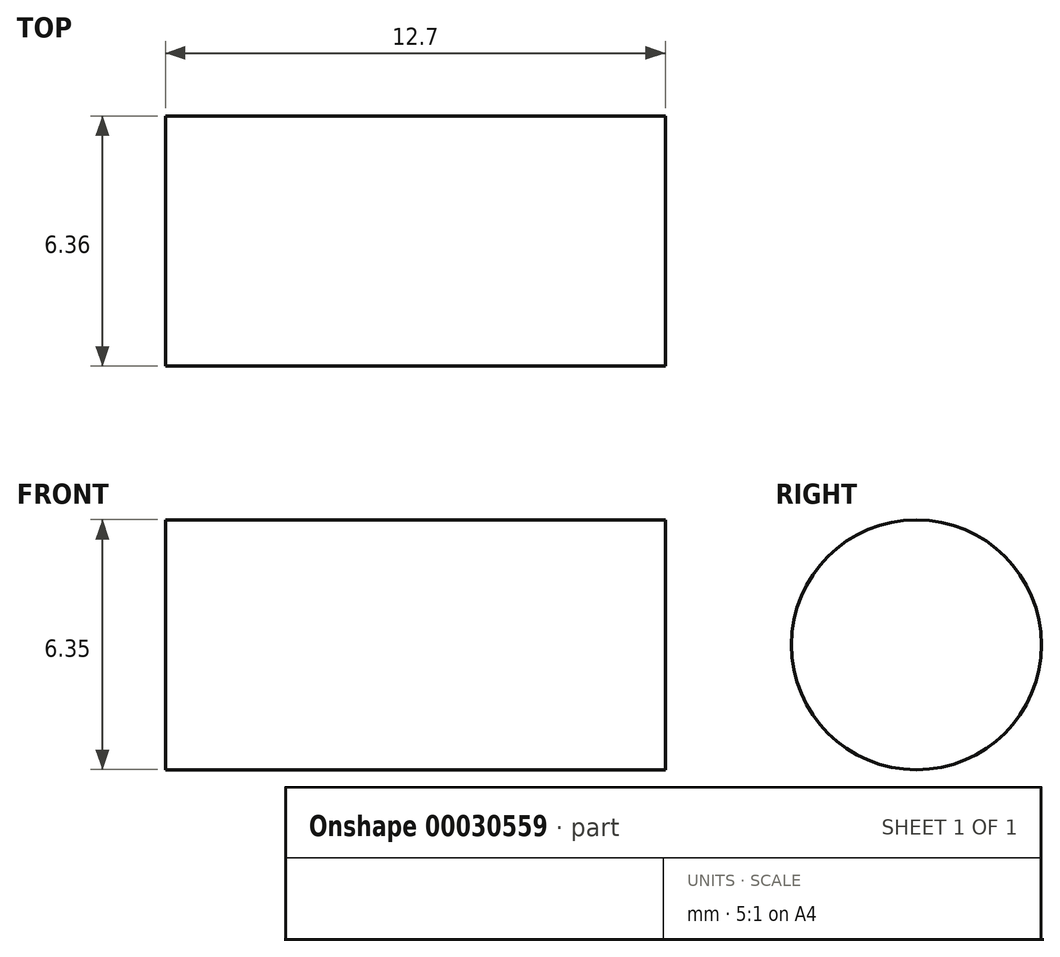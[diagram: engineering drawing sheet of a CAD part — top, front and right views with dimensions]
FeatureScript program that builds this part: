
annotation { "Feature Type Name" : "Feature", "Feature Type Description" : "" }
export const myFeature = defineFeature(function(context is Context, id is Id, definition is map)
    precondition{}
    {
        {
            var Q0;
            Q0=qCreatedBy(makeId("Front.planeOp"),FACE);
            var sketch = newSketch(context, id + "F0", { "sketchPlane" : qUnion([Q0])});
            skLineSegment(sketch, "E0", {"start": v(-13.32, -0.53) * mm, "end": v(-21.67, -0.53) * mm});
            skLineSegment(sketch, "E1", {"start": v(-13.32, 2.65) * mm, "end": v(-13.32, -0.53) * mm});
            skPoint(sketch, "E2.endSnap0", {"position": v(-0.62, -0.53) * mm});
            skLineSegment(sketch, "E2", {"start": v(-13.32, -0.53) * mm, "end": v(19.02, -0.53) * mm});
            skLineSegment(sketch, "E3.top", {"start": v(-13.32, 2.65) * mm, "end": v(-0.62, 2.65) * mm});
            skLineSegment(sketch, "E4", {"start": v(-0.62, 2.65) * mm, "end": v(-0.62, -0.53) * mm});
            skArc(sketch, "E5", {"start": v(9.62, -11.32) * mm, "mid": v(8.36, -8.28) * mm, "end": v(5.32, -7.02) * mm});
            skLineSegment(sketch, "E6", {"start": v(5.32, -11.32) * mm, "end": v(5.32, -5.59) * mm});
            skLineSegment(sketch, "E7", {"start": v(5.32, -5.59) * mm, "end": v(5.32, -11.32) * mm});
            skLineSegment(sketch, "E8", {"start": v(5.32, -11.32) * mm, "end": v(12, -11.32) * mm});
            skSolve(sketch);
        }
        {
            var Q0;
            {var subQ2=sQuery(id+"F0.wireOp",EDGE,"E1");Q0=makeQuery(id+"F0.imprint","IMPRINT",FACE,{"disambiguationData":[TD([[makeQuery(id+"F0.imprint","IMPRINT",EDGE,{"derivedFrom":subQ2}),1.0]])]});}
            var Q1;
            Q1=sQuery(id+"F0.wireOp",EDGE,"E0");
            revolve(context, id + "F1", {"entities" : qUnion([Q0]), "axis" : qUnion([Q1]), "revolveType" : RevolveType.FULL});
        }
    });
